# Revit family: Shower-Valve_Trim-KOHLER-MODULO-K-72802T_1
name_source: partatom
category: Plumbing Fixtures
revit_build: Autodesk Revit 2017 (Build: 20160225_1515(x64)
units: mm (PartAtom-declared; Revit-internal decimal feet)

## family parameters
Cut with Voids When Loaded = No
Host = Face
OmniClass Number = 23.31.25.00
OmniClass Title = Toilet and Bath Specialties
Part Type = Normal
Room Calculation Point = No
Round Connector Dimension = Use Diameter
Shared = No

## types (1)
- CP-Polished Chrome
    ADA Compliant = No
    Assembly Code = D2010700
    CW Connection = Yes
    Cold Water Inlet = Cold Water Inlet
    Date Modified = 07/28/2020
    Default Elevation = 42"
    Description = CLASSIC SHOWER ONLY TRIM AND VALVE-KELSTON
    Drain Included = No
    Finish = Kohler-Metal-CP-Polished_Chrome
    Flow Rate = 0 GPM
    HW Connection = Yes
    Handle Clearance = 3 3/16"
    Height = 7 1/16"
    Hot Water Inlet = Hot Water Inlet
    Length = 5 1/16"
    Manufacturer = KOHLER Co.
    Master Format 2014 = 10 28 00
    Master Format 2014 Name = Toilet, Bath, and Laundry Accessories
    Material = Premium Metal Construction
    Model = K-72802T-4-CP
    Pressure = 0.00 psi
    Product Name = MODULO
    Tempered Water Outlet 1 = Tempered Water Outlet 1
    Tempered Water Outlet 2 = Tempered Water Outlet 2
    Type = 1
    URL = http://www.kohler.com.cn
    Vent Connection = No
    Waste Connection = No
    Waste Water Outlet = Waste Water Outlet
    WaterSense Certified = No
    Width = 7 1/16"

## geometry (parser evidence)
native form markers: Sweep x4
no freeform markers — native parametric forms only
